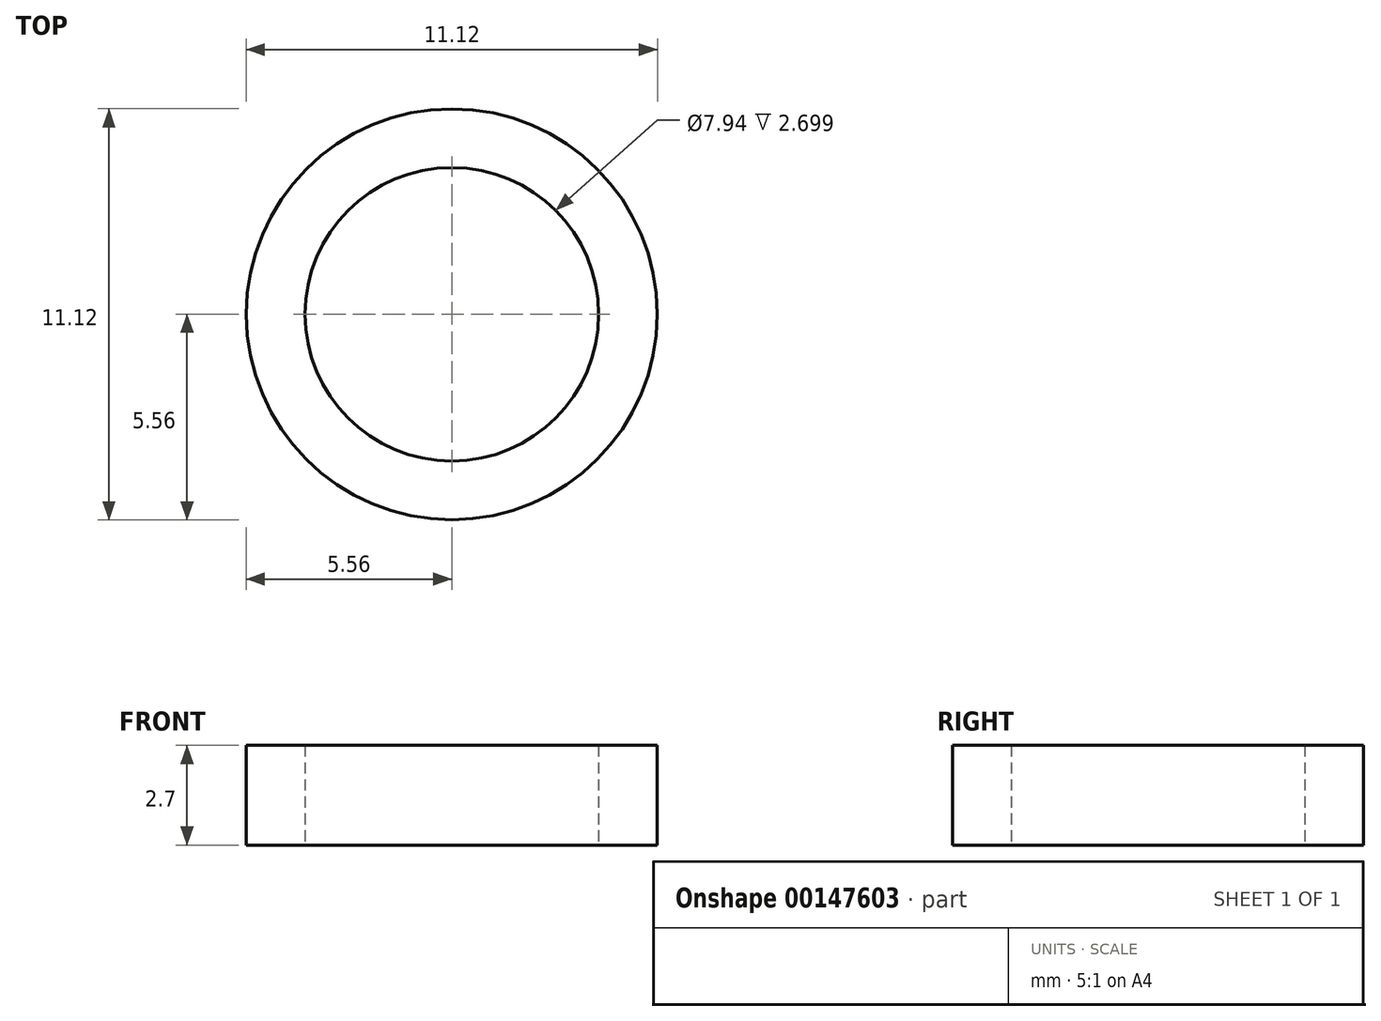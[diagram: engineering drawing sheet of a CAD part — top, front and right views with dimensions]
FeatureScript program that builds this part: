
annotation { "Feature Type Name" : "Feature", "Feature Type Description" : "" }
export const myFeature = defineFeature(function(context is Context, id is Id, definition is map)
    precondition{}
    {
        {
            var Q0;
            Q0=qCreatedBy(makeId("Top.planeOp"),FACE);
            var sketch = newSketch(context, id + "F0", { "sketchPlane" : qUnion([Q0])});
            skCircle(sketch, "E0", {"center": v(0, 0) * mm, "radius": 3.97 * mm});
            skCircle(sketch, "E1", {"center": v(0, 0) * mm, "radius": 5.56 * mm});
            skSolve(sketch);
        }
        {
            var Q0;
            Q0=makeQuery(id+"F0.imprint","IMPRINT",FACE,{"disambiguationData":[TD([[makeQuery(id+"F0.imprint","IMPRINT",EDGE,{"derivedFrom":sQuery(id+"F0.wireOp",EDGE,"E0")}),-1.0]])]});
            extrude(context, id + "F1", {"entities" : qUnion([Q0]), "depth" : 2.7 * mm});
        }
    });
